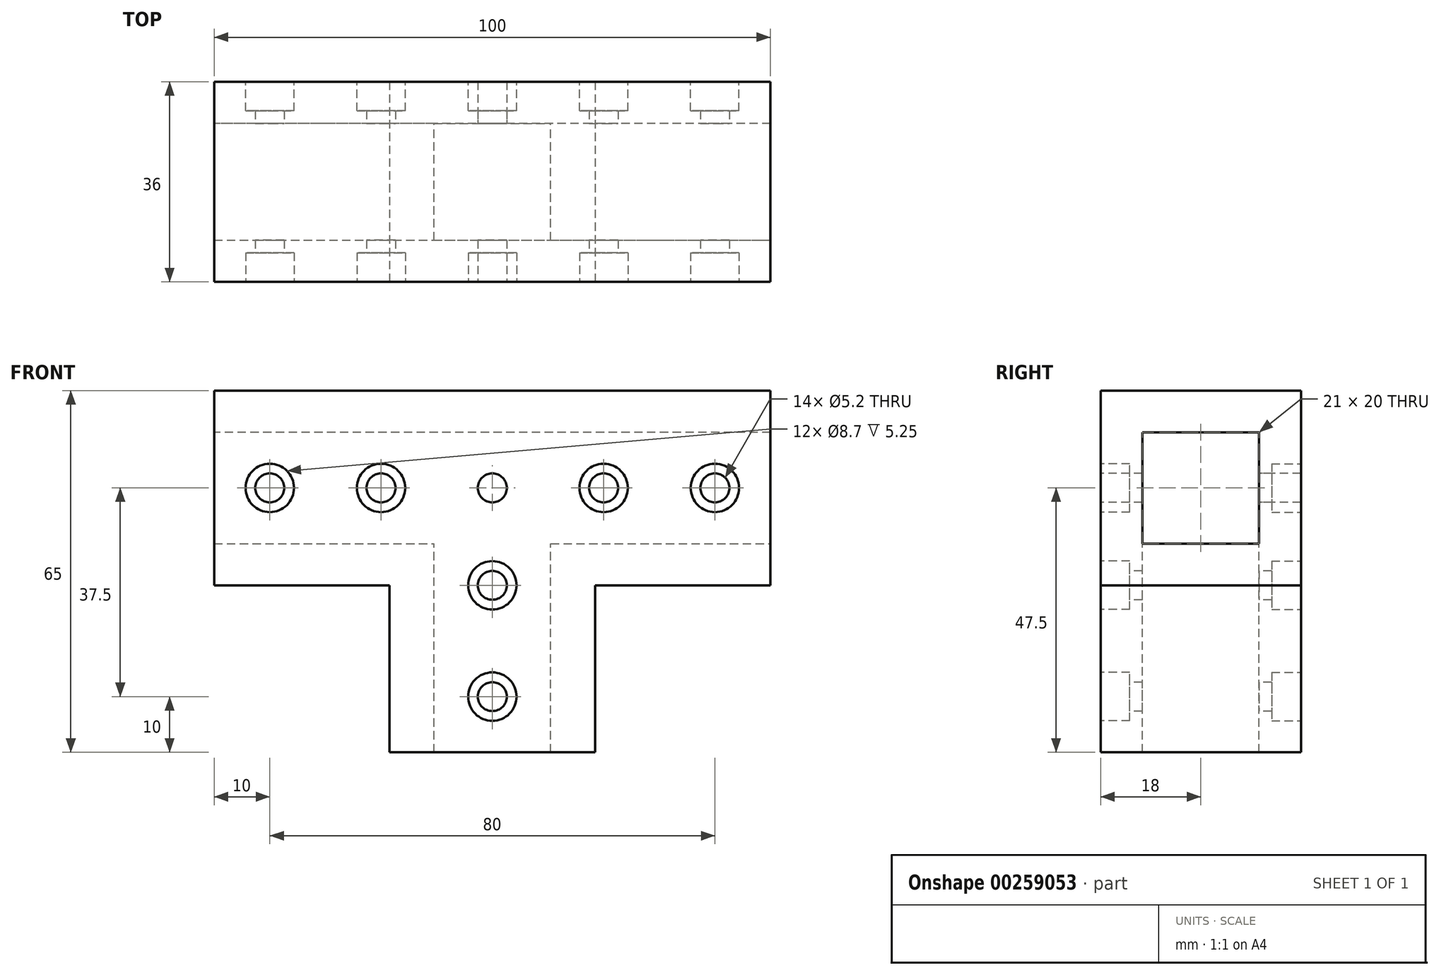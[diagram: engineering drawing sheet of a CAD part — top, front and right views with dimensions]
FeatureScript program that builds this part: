
annotation { "Feature Type Name" : "Feature", "Feature Type Description" : "" }
export const myFeature = defineFeature(function(context is Context, id is Id, definition is map)
    precondition{}
    {
        {
            var Q0;
            Q0=qCreatedBy(makeId("Top.planeOp"),FACE);
            var sketch = newSketch(context, id + "F0", { "sketchPlane" : qUnion([Q0])});
            skLineSegment(sketch, "E0.bottom", {"start": v(0, 0) * mm, "end": v(-100, 0) * mm});
            skLineSegment(sketch, "E0.top", {"start": v(0, 36) * mm, "end": v(-100, 36) * mm});
            skLineSegment(sketch, "E0.left", {"start": v(0, 0) * mm, "end": v(0, 36) * mm});
            skLineSegment(sketch, "E0.right", {"start": v(-100, 0) * mm, "end": v(-100, 36) * mm});
            skSolve(sketch);
        }
        {
            var Q0;
            Q0=makeQuery(id+"F0.imprint","IMPRINT",FACE,{"disambiguationData":[TD([[makeQuery(id+"F0.imprint","IMPRINT",EDGE,{"derivedFrom":sQuery(id+"F0.wireOp",EDGE,"E0.bottom")}),-1.0]])]});
            extrude(context, id + "F1", {"entities" : qUnion([Q0]), "depth" : 7.5 * mm});
        }
        {
            var Q0;
            Q0=makeQuery(id+"F1.opExtrude","CAP_FACE",FACE,{"disambiguationData":[OSD([sQuery(id+"F0.wireOp",EDGE,"E0.bottom"),sQuery(id+"F0.wireOp",EDGE,"E0.top"),sQuery(id+"F0.wireOp",EDGE,"E0.left"),sQuery(id+"F0.wireOp",EDGE,"E0.right")])],"isStart":true});
            var sketch = newSketch(context, id + "F2", { "sketchPlane" : qUnion([Q0])});
            skLineSegment(sketch, "E1.bottom", {"start": v(-100, 0) * mm, "end": v(0, 0) * mm});
            skLineSegment(sketch, "E1.top", {"start": v(-100, -7.5) * mm, "end": v(0, -7.5) * mm});
            skLineSegment(sketch, "E1.left", {"start": v(-100, 0) * mm, "end": v(-100, -7.5) * mm});
            skLineSegment(sketch, "E1.right", {"start": v(0, 0) * mm, "end": v(0, -7.5) * mm});
            skLineSegment(sketch, "E2.bottom", {"start": v(0, -36) * mm, "end": v(-100, -36) * mm});
            skLineSegment(sketch, "E2.top", {"start": v(0, -28.5) * mm, "end": v(-100, -28.5) * mm});
            skLineSegment(sketch, "E2.left", {"start": v(0, -36) * mm, "end": v(0, -28.5) * mm});
            skLineSegment(sketch, "E2.right", {"start": v(-100, -36) * mm, "end": v(-100, -28.5) * mm});
            skSolve(sketch);
        }
        {
            var Q0;
            Q0 = qSketchRegion(id + "F2", true);
            extrude(context, id + "F3", {"entities" : qUnion([Q0]), "operationType" : NewBodyOperationType.ADD, "depth" : 20 * mm});
        }
        {
            var Q0;
            Q0=makeQuery(id+"F3.opExtrude","CAP_FACE",FACE,{"disambiguationData":[OSD([sQuery(id+"F2.wireOp",EDGE,"E1.bottom"),sQuery(id+"F2.wireOp",EDGE,"E1.top"),sQuery(id+"F2.wireOp",EDGE,"E1.left"),sQuery(id+"F2.wireOp",EDGE,"E1.right")])],"isStart":false});
            var sketch = newSketch(context, id + "F4", { "sketchPlane" : qUnion([Q0])});
            skLineSegment(sketch, "E3.bottom", {"start": v(-100, 0) * mm, "end": v(0, 0) * mm});
            skLineSegment(sketch, "E3.top", {"start": v(-100, -36) * mm, "end": v(0, -36) * mm});
            skLineSegment(sketch, "E3.left", {"start": v(-100, 0) * mm, "end": v(-100, -36) * mm});
            skLineSegment(sketch, "E4.left", {"start": v(0, 0) * mm, "end": v(0, -36) * mm});
            skLineSegment(sketch, "E5.bottom", {"start": v(-60.5, -7.5) * mm, "end": v(-39.5, -7.5) * mm});
            skLineSegment(sketch, "E5.top", {"start": v(-60.5, -28.5) * mm, "end": v(-39.5, -28.5) * mm});
            skLineSegment(sketch, "E5.left", {"start": v(-60.5, -7.5) * mm, "end": v(-60.5, -28.5) * mm});
            skLineSegment(sketch, "E5.right", {"start": v(-39.5, -7.5) * mm, "end": v(-39.5, -28.5) * mm});
            skSolve(sketch);
        }
        {
            var Q0;
            Q0 = qSketchRegion(id + "F4", true);
            extrude(context, id + "F5", {"entities" : qUnion([Q0]), "operationType" : NewBodyOperationType.ADD, "depth" : 7.5 * mm});
        }
        {
            var Q0;
            Q0=makeQuery(id+"F5.opExtrude","CAP_FACE",FACE,{"disambiguationData":[OSD([sQuery(id+"F4.wireOp",EDGE,"E3.bottom"),sQuery(id+"F4.wireOp",EDGE,"E3.top"),sQuery(id+"F4.wireOp",EDGE,"E3.left"),sQuery(id+"F4.wireOp",EDGE,"E4.left"),sQuery(id+"F4.wireOp",EDGE,"E5.bottom"),sQuery(id+"F4.wireOp",EDGE,"E5.top"),sQuery(id+"F4.wireOp",EDGE,"E5.left"),sQuery(id+"F4.wireOp",EDGE,"E5.right")])],"isStart":false});
            var sketch = newSketch(context, id + "F6", { "sketchPlane" : qUnion([Q0])});
            skLineSegment(sketch, "E6.bottom", {"start": v(-68.5, -36) * mm, "end": v(-31.5, -36) * mm});
            skLineSegment(sketch, "E6.top", {"start": v(-68.5, 0) * mm, "end": v(-31.5, 0) * mm});
            skLineSegment(sketch, "E6.left", {"start": v(-68.5, -36) * mm, "end": v(-68.5, 0) * mm});
            skLineSegment(sketch, "E6.right", {"start": v(-31.5, -36) * mm, "end": v(-31.5, 0) * mm});
            skLineSegment(sketch, "E7.bottom", {"start": v(-39.5, -7.5) * mm, "end": v(-60.5, -7.5) * mm});
            skLineSegment(sketch, "E7.top", {"start": v(-39.5, -28.5) * mm, "end": v(-60.5, -28.5) * mm});
            skLineSegment(sketch, "E7.left", {"start": v(-39.5, -7.5) * mm, "end": v(-39.5, -28.5) * mm});
            skLineSegment(sketch, "E7.right", {"start": v(-60.5, -7.5) * mm, "end": v(-60.5, -28.5) * mm});
            skSolve(sketch);
        }
        {
            var Q0;
            Q0 = qSketchRegion(id + "F6", true);
            extrude(context, id + "F7", {"entities" : qUnion([Q0]), "operationType" : NewBodyOperationType.ADD, "depth" : 30 * mm});
        }
        {
            var Q0;
            Q0=makeQuery(id+"F7.boolean.opBoolean","MERGE",FACE,{"derivedFrom":[makeQuery(id+"F5.boolean.opBoolean","MERGE",FACE,{"derivedFrom":[makeQuery(id+"F3.boolean.opBoolean","MERGE",FACE,{"derivedFrom":[makeQuery(id+"F1.opExtrude","SWEPT_FACE",FACE,{"disambiguationData":[OSD([sQuery(id+"F0.wireOp",EDGE,"E0.bottom")])]}),makeQuery(id+"F3.opExtrude","SWEPT_FACE",FACE,{"disambiguationData":[OSD([sQuery(id+"F2.wireOp",EDGE,"E1.bottom")])]})]}),makeQuery(id+"F5.opExtrude","SWEPT_FACE",FACE,{"disambiguationData":[OSD([sQuery(id+"F4.wireOp",EDGE,"E3.bottom")])]})]}),makeQuery(id+"F7.opExtrude","SWEPT_FACE",FACE,{"disambiguationData":[OSD([sQuery(id+"F6.wireOp",EDGE,"E6.top")])]})]});
            var sketch = newSketch(context, id + "F8", { "sketchPlane" : qUnion([Q0])});
            skCircle(sketch, "E8", {"center": v(-90, -10) * mm, "radius": 2.6 * mm});
            skCircle(sketch, "E9", {"center": v(-50, -10) * mm, "radius": 2.6 * mm});
            skCircle(sketch, "E10", {"center": v(-10, -10) * mm, "radius": 2.6 * mm});
            skCircle(sketch, "E11", {"center": v(-30, -10) * mm, "radius": 2.6 * mm});
            skCircle(sketch, "E12", {"center": v(-70, -10) * mm, "radius": 2.6 * mm});
            skCircle(sketch, "E13", {"center": v(-50, -47.5) * mm, "radius": 2.6 * mm});
            skLineSegment(sketch, "E14", {"start": v(-100, -10) * mm, "end": v(0, -10) * mm, "construction": true});
            skLineSegment(sketch, "E15", {"start": v(-50, 7.5) * mm, "end": v(-50, -57.5) * mm, "construction": true});
            skLineSegment(sketch, "E16.bottom", {"start": v(-60, 0) * mm, "end": v(-40, 0) * mm, "construction": true});
            skLineSegment(sketch, "E16.top", {"start": v(-60, -57.5) * mm, "end": v(-40, -57.5) * mm, "construction": true});
            skLineSegment(sketch, "E16.left", {"start": v(-60, 0) * mm, "end": v(-60, -57.5) * mm, "construction": true});
            skLineSegment(sketch, "E16.right", {"start": v(-40, 0) * mm, "end": v(-40, -57.5) * mm, "construction": true});
            skCircle(sketch, "E17", {"center": v(-50, -27.5) * mm, "radius": 2.6 * mm});
            skSolve(sketch);
        }
        {
            var Q0;
            Q0 = qSketchRegion(id + "F8", true);
            extrude(context, id + "F9", {"entities" : qUnion([Q0]), "operationType" : NewBodyOperationType.REMOVE, "oppositeDirection" : true, "depth" : 60 * mm});
        }
        {
            var Q0;
            Q0=makeQuery(id+"F7.boolean.opBoolean","MERGE",FACE,{"derivedFrom":[makeQuery(id+"F5.boolean.opBoolean","MERGE",FACE,{"derivedFrom":[makeQuery(id+"F3.boolean.opBoolean","MERGE",FACE,{"derivedFrom":[makeQuery(id+"F1.opExtrude","SWEPT_FACE",FACE,{"disambiguationData":[OSD([sQuery(id+"F0.wireOp",EDGE,"E0.top")])]}),makeQuery(id+"F3.opExtrude","SWEPT_FACE",FACE,{"disambiguationData":[OSD([sQuery(id+"F2.wireOp",EDGE,"E2.bottom")])]})]}),makeQuery(id+"F5.opExtrude","SWEPT_FACE",FACE,{"disambiguationData":[OSD([sQuery(id+"F4.wireOp",EDGE,"E3.top")])]})]}),makeQuery(id+"F7.opExtrude","SWEPT_FACE",FACE,{"disambiguationData":[OSD([sQuery(id+"F6.wireOp",EDGE,"E6.bottom")])]})]});
            var sketch = newSketch(context, id + "F10", { "sketchPlane" : qUnion([Q0])});
            skCircle(sketch, "E18", {"center": v(50, -47.5) * mm, "radius": 4.35 * mm});
            skCircle(sketch, "E19", {"center": v(50, -27.5) * mm, "radius": 4.35 * mm});
            skCircle(sketch, "E20", {"center": v(90, -10) * mm, "radius": 4.35 * mm});
            skCircle(sketch, "E21", {"center": v(70, -10) * mm, "radius": 4.35 * mm});
            skCircle(sketch, "E22", {"center": v(30, -10) * mm, "radius": 4.35 * mm});
            skCircle(sketch, "E23", {"center": v(10, -10) * mm, "radius": 4.35 * mm});
            skSolve(sketch);
        }
        {
            var Q0;
            Q0 = qSketchRegion(id + "F10", true);
            extrude(context, id + "F11", {"entities" : qUnion([Q0]), "operationType" : NewBodyOperationType.REMOVE, "oppositeDirection" : true, "depth" : 5.25 * mm});
        }
        {
            var Q0;
            Q0=makeQuery(id+"F7.boolean.opBoolean","MERGE",FACE,{"derivedFrom":[makeQuery(id+"F5.boolean.opBoolean","MERGE",FACE,{"derivedFrom":[makeQuery(id+"F3.boolean.opBoolean","MERGE",FACE,{"derivedFrom":[makeQuery(id+"F1.opExtrude","SWEPT_FACE",FACE,{"disambiguationData":[OSD([sQuery(id+"F0.wireOp",EDGE,"E0.bottom")])]}),makeQuery(id+"F3.opExtrude","SWEPT_FACE",FACE,{"disambiguationData":[OSD([sQuery(id+"F2.wireOp",EDGE,"E1.bottom")])]})]}),makeQuery(id+"F5.opExtrude","SWEPT_FACE",FACE,{"disambiguationData":[OSD([sQuery(id+"F4.wireOp",EDGE,"E3.bottom")])]})]}),makeQuery(id+"F7.opExtrude","SWEPT_FACE",FACE,{"disambiguationData":[OSD([sQuery(id+"F6.wireOp",EDGE,"E6.top")])]})]});
            var sketch = newSketch(context, id + "F12", { "sketchPlane" : qUnion([Q0])});
            skCircle(sketch, "E24", {"center": v(-90, -10) * mm, "radius": 4.35 * mm});
            skCircle(sketch, "E25", {"center": v(-70, -10) * mm, "radius": 4.35 * mm});
            skCircle(sketch, "E26", {"center": v(-30, -10) * mm, "radius": 4.35 * mm});
            skCircle(sketch, "E27", {"center": v(-10, -10) * mm, "radius": 4.35 * mm});
            skCircle(sketch, "E28", {"center": v(-50, -27.5) * mm, "radius": 4.35 * mm});
            skCircle(sketch, "E29", {"center": v(-50, -47.5) * mm, "radius": 4.35 * mm});
            skSolve(sketch);
        }
        {
            var Q0;
            Q0 = qSketchRegion(id + "F12", true);
            extrude(context, id + "F13", {"entities" : qUnion([Q0]), "operationType" : NewBodyOperationType.REMOVE, "oppositeDirection" : true, "depth" : 5.25 * mm});
        }
    });
